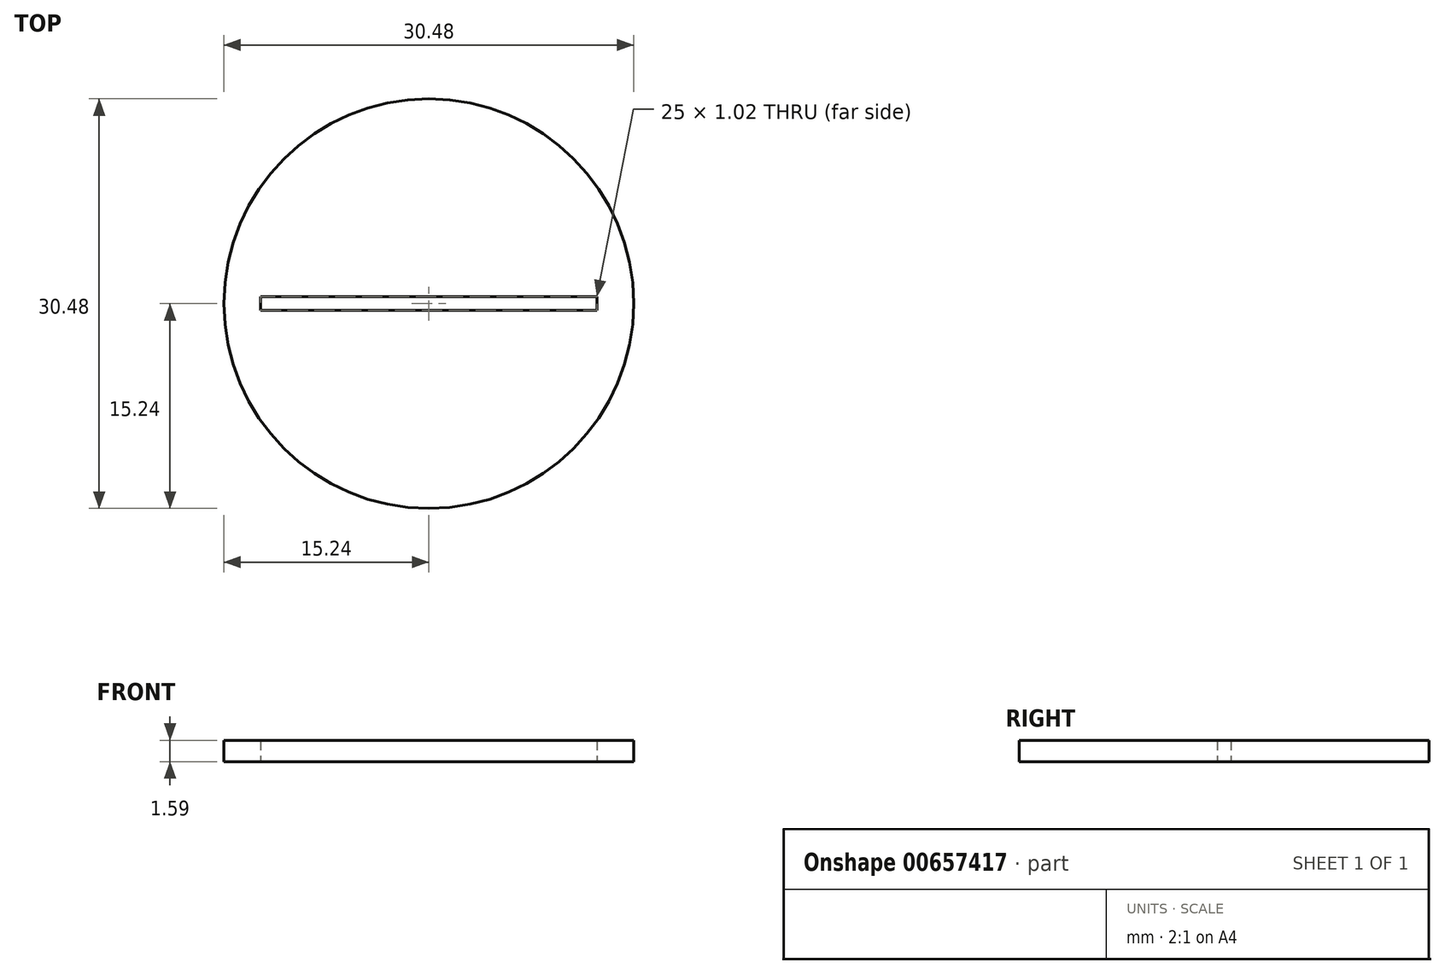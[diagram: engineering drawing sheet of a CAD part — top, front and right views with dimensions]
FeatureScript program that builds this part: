
annotation { "Feature Type Name" : "Feature", "Feature Type Description" : "" }
export const myFeature = defineFeature(function(context is Context, id is Id, definition is map)
    precondition{}
    {
        {
            var Q0;
            Q0=qCreatedBy(makeId("Top.planeOp"),FACE);
            var sketch = newSketch(context, id + "F0", { "sketchPlane" : qUnion([Q0])});
            skCircle(sketch, "E0", {"center": v(0, 0) * mm, "radius": 15.24 * mm});
            skLineSegment(sketch, "E1.bottom", {"start": v(12.5, 0.5) * mm, "end": v(-12.5, 0.5) * mm});
            skLineSegment(sketch, "E1.top", {"start": v(12.5, -0.5) * mm, "end": v(-12.5, -0.5) * mm});
            skLineSegment(sketch, "E1.left", {"start": v(12.5, 0.5) * mm, "end": v(12.5, -0.5) * mm});
            skLineSegment(sketch, "E1.right", {"start": v(-12.5, 0.5) * mm, "end": v(-12.5, -0.5) * mm});
            skSolve(sketch);
        }
        {
            var Q0;
            Q0=makeQuery(id+"F0.imprint","IMPRINT",FACE,{"disambiguationData":[TD([[makeQuery(id+"F0.imprint","IMPRINT",EDGE,{"derivedFrom":sQuery(id+"F0.wireOp",EDGE,"E0")}),1.0]])]});
            extrude(context, id + "F1", {"entities" : qUnion([Q0]), "depth" : 1.59 * mm, "offsetDistance" : 25.4 * mm});
        }
    });
